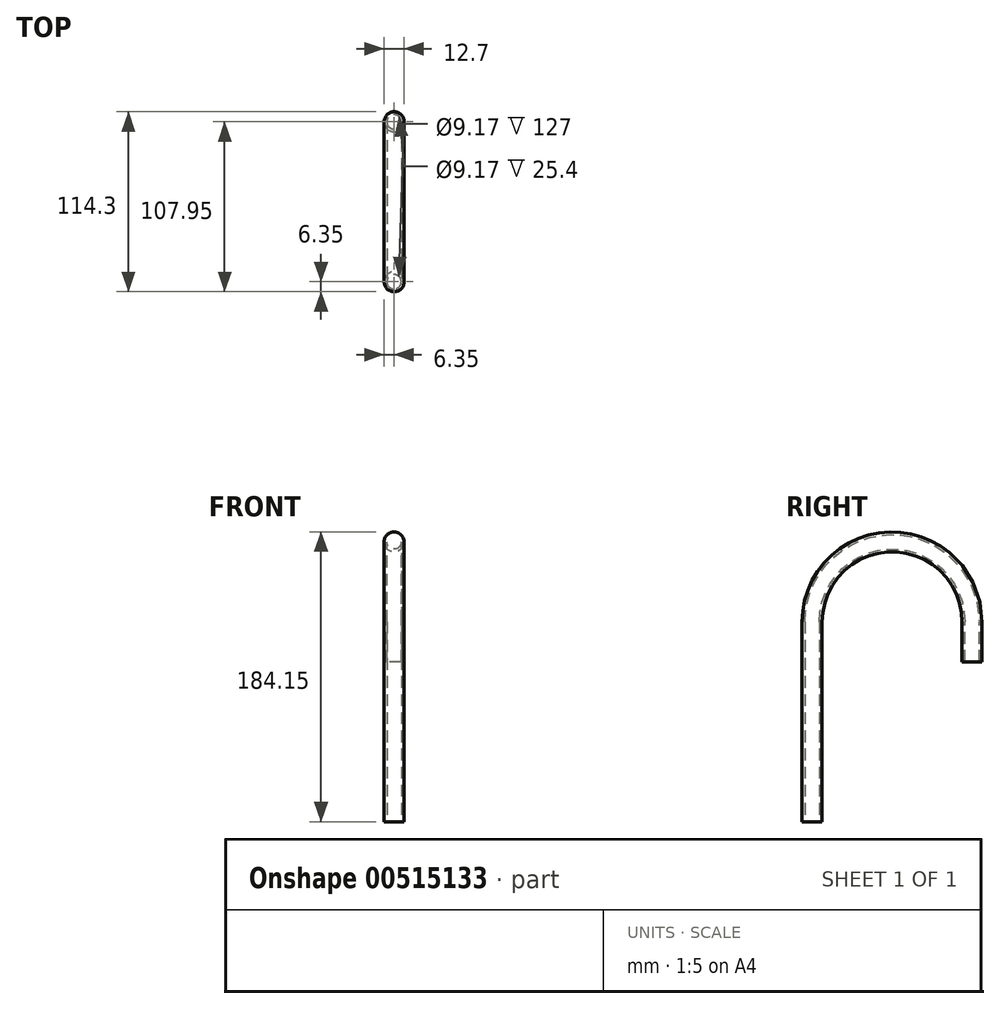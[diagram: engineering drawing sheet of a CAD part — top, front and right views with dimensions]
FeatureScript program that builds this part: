
annotation { "Feature Type Name" : "Feature", "Feature Type Description" : "" }
export const myFeature = defineFeature(function(context is Context, id is Id, definition is map)
    precondition{}
    {
        {
            var Q0;
            Q0=qCreatedBy(makeId("Right.planeOp"),FACE);
            var sketch = newSketch(context, id + "F0", { "sketchPlane" : qUnion([Q0])});
            skLineSegment(sketch, "E0", {"start": v(0, 0) * mm, "end": v(0, 25.4) * mm});
            skArc(sketch, "E1", {"start": v(0, 25.4) * mm, "mid": v(-50.8, 76.2) * mm, "end": v(-101.6, 25.4) * mm});
            skLineSegment(sketch, "E2", {"start": v(-101.6, 25.4) * mm, "end": v(-101.6, -101.6) * mm});
            skSolve(sketch);
        }
        {
            var Q0;
            Q0=qCreatedBy(makeId("Top.planeOp"),FACE);
            var sketch = newSketch(context, id + "F1", { "sketchPlane" : qUnion([Q0])});
            skCircle(sketch, "E3", {"center": v(0, 0) * mm, "radius": 6.35 * mm});
            skCircle(sketch, "E4", {"center": v(0, 0) * mm, "radius": 4.59 * mm});
            skSolve(sketch);
        }
        {
            var Q0;
            Q0=makeQuery(id+"F1.imprint","IMPRINT",FACE,{"disambiguationData":[TD([[makeQuery(id+"F1.imprint","IMPRINT",EDGE,{"derivedFrom":sQuery(id+"F1.wireOp",EDGE,"E3")}),1.0]])]});
            var Q1;
            Q1=sQuery(id+"F0.wireOp",EDGE,"E0");
            var Q2;
            Q2=sQuery(id+"F0.wireOp",EDGE,"E1");
            var Q3;
            Q3=sQuery(id+"F0.wireOp",EDGE,"E2");
            sweep(context, id + "F2", {"profiles" : qUnion([Q0]), "path" : qUnion([Q1, Q2, Q3])});
        }
    });
